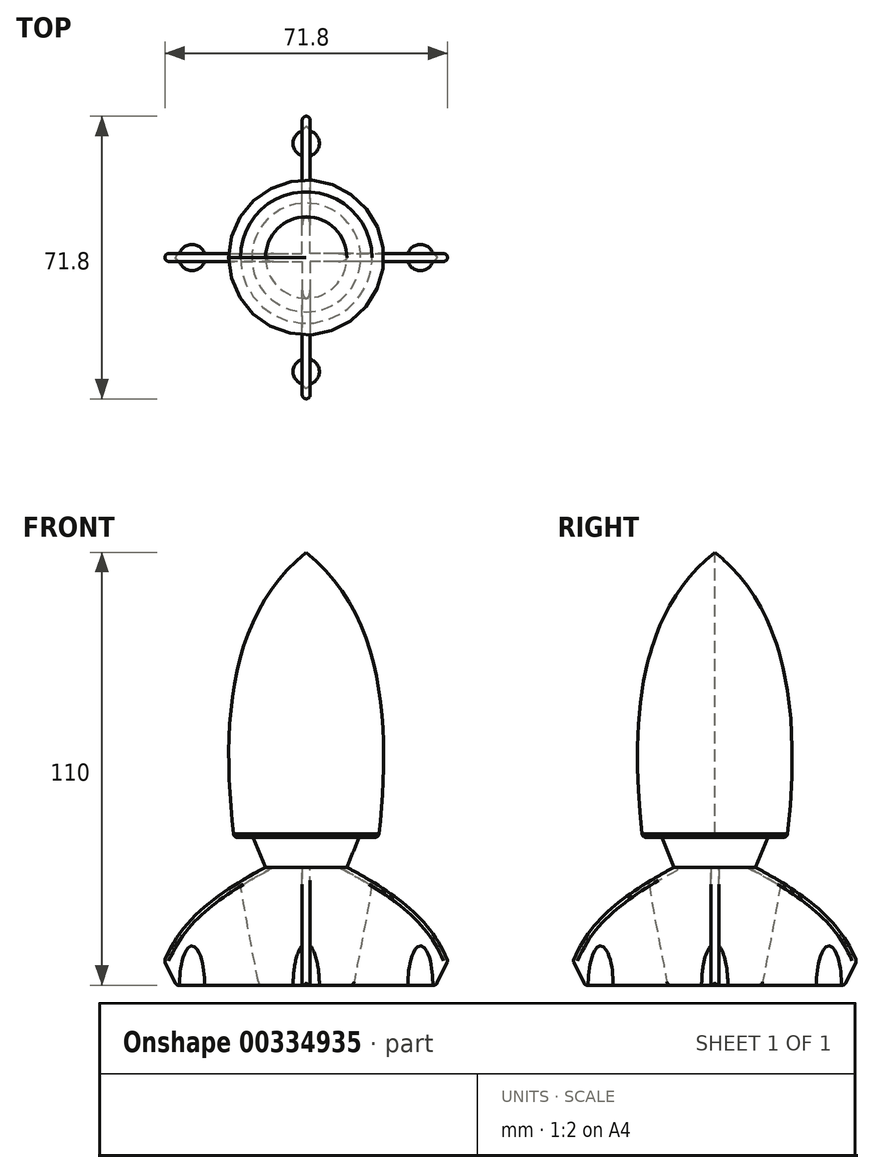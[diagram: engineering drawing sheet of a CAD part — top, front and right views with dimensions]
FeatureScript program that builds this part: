
annotation { "Feature Type Name" : "Feature", "Feature Type Description" : "" }
export const myFeature = defineFeature(function(context is Context, id is Id, definition is map)
    precondition{}
    {
        {
            var Q0;
            Q0=qCreatedBy(makeId("Front.planeOp"),FACE);
            var sketch = newSketch(context, id + "F0", { "sketchPlane" : qUnion([Q0])});
            skLineSegment(sketch, "E0", {"start": v(0, -72.35) * mm, "end": v(0, 89.92) * mm, "construction": true});
            skFitSpline(sketch, "E1", {"points": [v(-12, 0) * mm, v(0, 110) * mm], "startDerivative": vector(-16.04, 87.03) * mm, "endDerivative": vector(93.37, 74.04) * mm});
            skLineSegment(sketch, "E2", {"start": v(-12, 0) * mm, "end": v(0, 0) * mm});
            skLineSegment(sketch, "E3", {"start": v(0, 0) * mm, "end": v(0, 110) * mm});
            skSolve(sketch);
        }
        {
            var Q0;
            Q0 = qSketchRegion(id + "F0", true);
            var Q1;
            Q1=sQuery(id+"F0.wireOp",EDGE,"E3");
            revolve(context, id + "F1", {"entities" : qUnion([Q0]), "axis" : qUnion([Q1]), "revolveType" : RevolveType.FULL});
        }
        {
            var Q0;
            Q0=qCreatedBy(makeId("Top.planeOp"),FACE);
            var sketch = newSketch(context, id + "F2", { "sketchPlane" : qUnion([Q0])});
            skLineSegment(sketch, "E4", {"start": v(-36, 1) * mm, "end": v(-1, 1) * mm});
            skLineSegment(sketch, "E5", {"start": v(-1, 1) * mm, "end": v(-1, 36) * mm});
            skLineSegment(sketch, "E6.MirrorCS", {"start": v(1, 1) * mm, "end": v(1, 36) * mm});
            skLineSegment(sketch, "E7.MirrorCS", {"start": v(36, 1) * mm, "end": v(1, 1) * mm});
            skLineSegment(sketch, "E8.MirrorCS", {"start": v(36, -1) * mm, "end": v(1, -1) * mm});
            skLineSegment(sketch, "E9.MirrorCS", {"start": v(1, -1) * mm, "end": v(1, -36) * mm});
            skLineSegment(sketch, "E10.MirrorCS", {"start": v(-1, -1) * mm, "end": v(-1, -36) * mm});
            skLineSegment(sketch, "E11.MirrorCS", {"start": v(-36, -1) * mm, "end": v(-1, -1) * mm});
            skLineSegment(sketch, "E12", {"start": v(-36, 1) * mm, "end": v(-36, -1) * mm});
            skLineSegment(sketch, "E13", {"start": v(-1, 36) * mm, "end": v(1, 36) * mm});
            skLineSegment(sketch, "E14", {"start": v(36, 1) * mm, "end": v(36, -1) * mm});
            skLineSegment(sketch, "E15", {"start": v(-1, -36) * mm, "end": v(1, -36) * mm});
            skSolve(sketch);
        }
        {
            var Q0;
            Q0 = qSketchRegion(id + "F2", true);
            extrude(context, id + "F3", {"entities" : qUnion([Q0]), "depth" : 30 * mm});
        }
        {
            var Q0;
            Q0=makeQuery(id+"F3.opExtrude","SWEPT_FACE",FACE,{"disambiguationData":[OSD([sQuery(id+"F2.wireOp",EDGE,"E4")])]});
            var Q1;
            Q1=makeQuery(id+"F3.opExtrude","SWEPT_FACE",FACE,{"disambiguationData":[OSD([sQuery(id+"F2.wireOp",EDGE,"E11.MirrorCS")])]});
            cPlane(context, id + "F4", {"entities" : qUnion([Q0, Q1]), "cplaneType" : CPlaneType.MID_PLANE, "offset" : 25 * mm, "width" : 150 * mm, "height" : 150 * mm});
        }
        {
            var Q0;
            Q0=qCreatedBy(id+"F4.planeOp",FACE);
            var sketch = newSketch(context, id + "F5", { "sketchPlane" : qUnion([Q0])});
            skLineSegment(sketch, "E16.0", {"start": v(36, 30) * mm, "end": v(1, 30) * mm, "construction": true});
            skPoint(sketch, "E17.0", {"position": v(36, 15) * mm});
            skLineSegment(sketch, "E18.0", {"start": v(36, 30) * mm, "end": v(36, 0) * mm, "construction": true});
            skFitSpline(sketch, "E19", {"points": [v(10.33, 30) * mm, v(36, 6.2) * mm], "startDerivative": vector(44.7, -24.32) * mm, "endDerivative": vector(12.18, -28.76) * mm});
            skLineSegment(sketch, "E20", {"start": v(36, 6.2) * mm, "end": v(32.98, 0) * mm});
            skLineSegment(sketch, "E21", {"start": v(32.98, 0) * mm, "end": v(38.82, -1.11) * mm});
            skLineSegment(sketch, "E22", {"start": v(38.82, -1.11) * mm, "end": v(51.8, 29.3) * mm});
            skLineSegment(sketch, "E23", {"start": v(51.8, 29.3) * mm, "end": v(13.81, 38.45) * mm});
            skLineSegment(sketch, "E24", {"start": v(13.81, 38.45) * mm, "end": v(10.33, 30) * mm});
            skLineSegment(sketch, "E25", {"start": v(0, 0) * mm, "end": v(0, 36.44) * mm, "construction": true});
            skSolve(sketch);
        }
        {
            var Q0;
            Q0 = qSketchRegion(id + "F5", true);
            var Q1;
            Q1=sQuery(id+"F5.wireOp",EDGE,"E25");
            revolve(context, id + "F6", {"operationType" : NewBodyOperationType.REMOVE, "entities" : qUnion([Q0]), "axis" : qUnion([Q1]), "revolveType" : RevolveType.FULL, "oppositeDirection" : true});
        }
        {
            var Q0;
            {var subQ1=sQuery(id+"F2.wireOp",EDGE,"E5");Q0=makeQuery(id+"F6.boolean.opBoolean","COPY",FACE,{"disambiguationData":[TD([makeQuery(id+"F3.opExtrude","SWEPT_FACE",FACE,{"disambiguationData":[OSD([subQ1])]})])],"derivedFrom":makeQuery(id+"F6.opRevolve","SWEPT_FACE",FACE,{"disambiguationData":[OSD([sQuery(id+"F5.wireOp",EDGE,"E19")])]})});}
            var Q1;
            {var subQ1=sQuery(id+"F2.wireOp",EDGE,"E5");Q1=makeQuery(id+"F6.boolean.opBoolean","COPY",FACE,{"disambiguationData":[TD([makeQuery(id+"F3.opExtrude","SWEPT_FACE",FACE,{"disambiguationData":[OSD([subQ1])]})])],"derivedFrom":makeQuery(id+"F6.opRevolve","SWEPT_FACE",FACE,{"disambiguationData":[OSD([sQuery(id+"F5.wireOp",EDGE,"E20")])]})});}
            var Q2;
            {var subQ0=sQuery(id+"F2.wireOp",EDGE,"E4");Q2=makeQuery(id+"F6.boolean.opBoolean","COPY",FACE,{"disambiguationData":[TD([makeQuery(id+"F3.opExtrude","SWEPT_FACE",FACE,{"disambiguationData":[OSD([subQ0])]})])],"derivedFrom":makeQuery(id+"F6.opRevolve","SWEPT_FACE",FACE,{"disambiguationData":[OSD([sQuery(id+"F5.wireOp",EDGE,"E19")])]})});}
            var Q3;
            {var subQ0=sQuery(id+"F2.wireOp",EDGE,"E4");Q3=makeQuery(id+"F6.boolean.opBoolean","COPY",FACE,{"disambiguationData":[TD([makeQuery(id+"F3.opExtrude","SWEPT_FACE",FACE,{"disambiguationData":[OSD([subQ0])]})])],"derivedFrom":makeQuery(id+"F6.opRevolve","SWEPT_FACE",FACE,{"disambiguationData":[OSD([sQuery(id+"F5.wireOp",EDGE,"E20")])]})});}
            var Q4;
            {var subQ1=sQuery(id+"F2.wireOp",EDGE,"E9.MirrorCS");Q4=makeQuery(id+"F6.boolean.opBoolean","COPY",FACE,{"disambiguationData":[TD([makeQuery(id+"F3.opExtrude","SWEPT_FACE",FACE,{"disambiguationData":[OSD([subQ1])]})])],"derivedFrom":makeQuery(id+"F6.opRevolve","SWEPT_FACE",FACE,{"disambiguationData":[OSD([sQuery(id+"F5.wireOp",EDGE,"E19")])]})});}
            var Q5;
            {var subQ1=sQuery(id+"F2.wireOp",EDGE,"E9.MirrorCS");Q5=makeQuery(id+"F6.boolean.opBoolean","COPY",FACE,{"disambiguationData":[TD([makeQuery(id+"F3.opExtrude","SWEPT_FACE",FACE,{"disambiguationData":[OSD([subQ1])]})])],"derivedFrom":makeQuery(id+"F6.opRevolve","SWEPT_FACE",FACE,{"disambiguationData":[OSD([sQuery(id+"F5.wireOp",EDGE,"E20")])]})});}
            var Q6;
            {var subQ1=sQuery(id+"F2.wireOp",EDGE,"E7.MirrorCS");Q6=makeQuery(id+"F6.boolean.opBoolean","COPY",FACE,{"disambiguationData":[TD([makeQuery(id+"F3.opExtrude","SWEPT_FACE",FACE,{"disambiguationData":[OSD([subQ1])]})])],"derivedFrom":makeQuery(id+"F6.opRevolve","SWEPT_FACE",FACE,{"disambiguationData":[OSD([sQuery(id+"F5.wireOp",EDGE,"E19")])]})});}
            var Q7;
            {var subQ1=sQuery(id+"F2.wireOp",EDGE,"E7.MirrorCS");Q7=makeQuery(id+"F6.boolean.opBoolean","COPY",FACE,{"disambiguationData":[TD([makeQuery(id+"F3.opExtrude","SWEPT_FACE",FACE,{"disambiguationData":[OSD([subQ1])]})])],"derivedFrom":makeQuery(id+"F6.opRevolve","SWEPT_FACE",FACE,{"disambiguationData":[OSD([sQuery(id+"F5.wireOp",EDGE,"E20")])]})});}
            fillet(context, id + "F7", {"entities" : qUnion([Q0, Q1, Q2, Q3, Q4, Q5, Q6, Q7]), "radius" : 1 * mm, "tangentPropagation" : true, "allowEdgeOverflow" : false});
        }
        {
            var Q0;
            Q0=makeQuery(id+"F1.opRevolve","SWEPT_FACE",FACE,{"disambiguationData":[OSD([sQuery(id+"F0.wireOp",EDGE,"E1")])]});
            fillet(context, id + "F8", {"entities" : qUnion([Q0]), "radius" : 1 * mm, "tangentPropagation" : true, "allowEdgeOverflow" : false});
        }
        {
            var Q0;
            Q0=qCreatedBy(id+"F4.planeOp",FACE);
            cPlane(context, id + "F9", {"entities" : qUnion([Q0]), "cplaneType" : CPlaneType.OFFSET, "offset" : 29 * mm, "width" : 150 * mm, "height" : 150 * mm});
        }
        {
            var Q0;
            Q0=qCreatedBy(id+"F9.planeOp",FACE);
            var sketch = newSketch(context, id + "F10", { "sketchPlane" : qUnion([Q0])});
            skLineSegment(sketch, "E26", {"start": v(0, 0) * mm, "end": v(0, 25.48) * mm, "construction": true});
            skLineSegment(sketch, "E27", {"start": v(0, 0) * mm, "end": v(3.33, 0) * mm});
            skFitSpline(sketch, "E28", {"points": [v(3.33, 0) * mm, v(0, 10.84) * mm], "startDerivative": vector(0.06, 6.12) * mm, "endDerivative": vector(-9.17, 4.31) * mm});
            skLineSegment(sketch, "E29", {"start": v(0, 0) * mm, "end": v(0, 10.84) * mm});
            skSolve(sketch);
        }
        {
            var Q0;
            Q0 = qSketchRegion(id + "F10", true);
            var Q1;
            Q1=sQuery(id+"F10.wireOp",EDGE,"E29");
            revolve(context, id + "F11", {"entities" : qUnion([Q0]), "axis" : qUnion([Q1]), "revolveType" : RevolveType.FULL});
        }
        {
            var Q0;
            Q0=makeQuery(id+"F11.opRevolve","SWEPT_BODY",BODY,{"disambiguationData":[OSD([sQuery(id+"F10.wireOp",EDGE,"E27"),sQuery(id+"F10.wireOp",EDGE,"E28"),sQuery(id+"F10.wireOp",EDGE,"E29")])]});
            var Q1;
            Q1=qCreatedBy(makeId("Front.planeOp"),FACE);
            mirror(context, id + "F12", {"entities" : qUnion([Q0]), "mirrorPlane" : qUnion([Q1])});
        }
        {
            var Q0;
            Q0=qCreatedBy(makeId("Top.planeOp"),FACE);
            var sketch = newSketch(context, id + "F13", { "sketchPlane" : qUnion([Q0])});
            skLineSegment(sketch, "E30", {"start": v(0, 0) * mm, "end": v(43.2, 43.2) * mm});
            skSolve(sketch);
        }
        {
            var Q0;
            Q0=sQuery(id+"F13.wireOp",VERTEX,"E30.start");
            var Q1;
            Q1=sQuery(id+"F13.wireOp",VERTEX,"E30.end");
            var Q2;
            Q2=makeQuery(id+"F1.opRevolve","SWEPT_VERTEX",VERTEX,{"disambiguationData":[OSD([sQuery(id+"F0.wireOp",EDGE,"E1"),sQuery(id+"F0.wireOp",EDGE,"E3")])]});
            cPlane(context, id + "F14", {"entities" : qUnion([Q0, Q1, Q2]), "cplaneType" : CPlaneType.THREE_POINT, "offset" : 25 * mm, "width" : 150 * mm, "height" : 150 * mm});
        }
        {
            var Q0;
            Q0=makeQuery(id+"F11.opRevolve","SWEPT_BODY",BODY,{"disambiguationData":[OSD([sQuery(id+"F10.wireOp",EDGE,"E27"),sQuery(id+"F10.wireOp",EDGE,"E28"),sQuery(id+"F10.wireOp",EDGE,"E29")])]});
            var Q1;
            Q1=qCreatedBy(id+"F14.planeOp",FACE);
            mirror(context, id + "F15", {"operationType" : NewBodyOperationType.ADD, "entities" : qUnion([Q0]), "mirrorPlane" : qUnion([Q1])});
        }
        {
            var Q0;
            Q0=makeQuery(id+"F12.opPattern","COPY",BODY,{"derivedFrom":makeQuery(id+"F11.opRevolve","SWEPT_BODY",BODY,{"disambiguationData":[OSD([sQuery(id+"F10.wireOp",EDGE,"E27"),sQuery(id+"F10.wireOp",EDGE,"E28"),sQuery(id+"F10.wireOp",EDGE,"E29")])]}),"instanceName":"1"});
            var Q1;
            Q1=qCreatedBy(id+"F14.planeOp",FACE);
            mirror(context, id + "F16", {"operationType" : NewBodyOperationType.ADD, "entities" : qUnion([Q0]), "mirrorPlane" : qUnion([Q1])});
        }
    });
